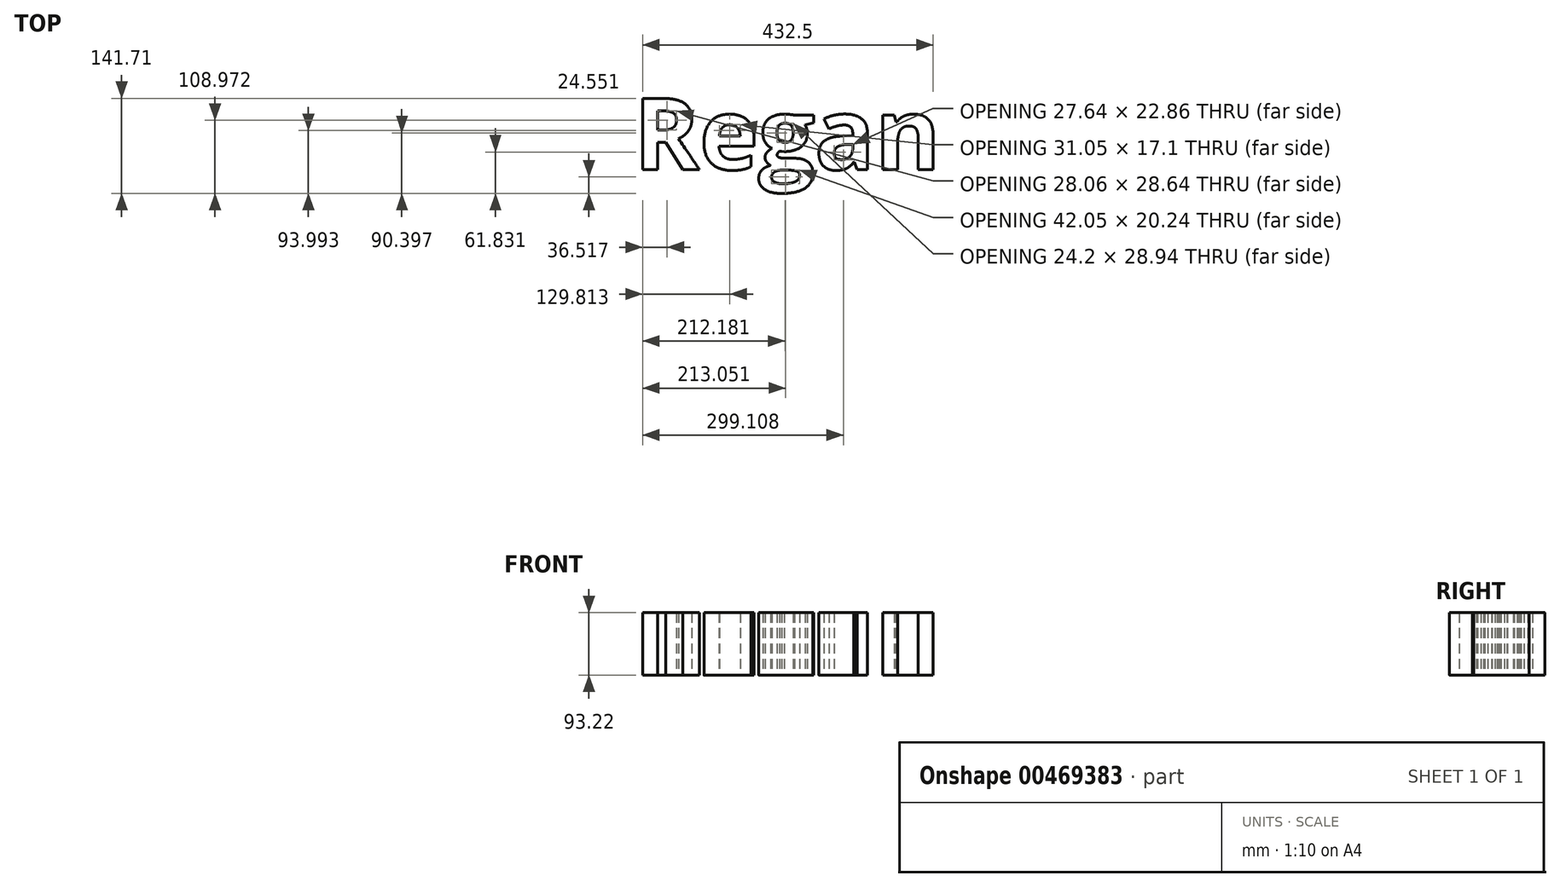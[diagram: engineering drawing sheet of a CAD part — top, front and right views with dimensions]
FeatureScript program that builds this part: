
annotation { "Feature Type Name" : "Feature", "Feature Type Description" : "" }
export const myFeature = defineFeature(function(context is Context, id is Id, definition is map)
    precondition{}
    {
        {
            var Q0;
            Q0=qCreatedBy(makeId("Top.planeOp"),FACE);
            var sketch = newSketch(context, id + "F0", { "sketchPlane" : qUnion([Q0])});
            skText(sketch, "E0", { "text": "Regan", "fontName": "OpenSans-Bold.ttf"});
            const initialGuessF0  = {"E0": [-0.1422, -0.0527, 1, 0, 0.10693]};
            skSetInitialGuess(sketch, initialGuessF0);
            skSolve(sketch);
        }
        {
            var Q0;
            Q0 = qSketchRegion(id + "F0", true);
            extrude(context, id + "F1", {"entities" : qUnion([Q0]), "depth" : 93.22 * mm, "offsetDistance" : 25.4 * mm});
        }
    });
